# Revit family: Shutters
name_source: partatom
category: Generic Models
revit_build: Autodesk Revit 2016 (Build: 20150220_1215(x64)
units: mm (PartAtom-declared; Revit-internal decimal feet)

## family parameters
Always vertical = Yes
Can host rebar = No
Cut with Voids When Loaded = No
Host = Wall
Part Type = Normal
Room Calculation Point = No
Round Connector Dimension = Use Diameter
Shared = No

## types (2) — shared parameters
Internal Dimension = 2924 mm  [stored 9.59318 ft]
Panel Width = 730 mm  [stored 2.39501 ft]
Width = 3000 mm  [stored 9.84252 ft]

## per-type parameters (varying)
| type | Blade Angle | Height | Open Angle | Panel Height |
| 3000 x 2465 | 90.00° | 2465 mm | 35.00° | 2427 mm |
| 2000 x 1932 | 45.00° | 2500 mm  [stored 8.2021 ft] | 80.00° | 2462 mm  [stored 8.07743 ft] |

note: [stored X ft] marks values corroborated as IEEE doubles in the binary element streams (Revit-internal decimal feet)

## geometry (parser evidence)
native form markers: Sweep x34
no freeform markers — native parametric forms only
